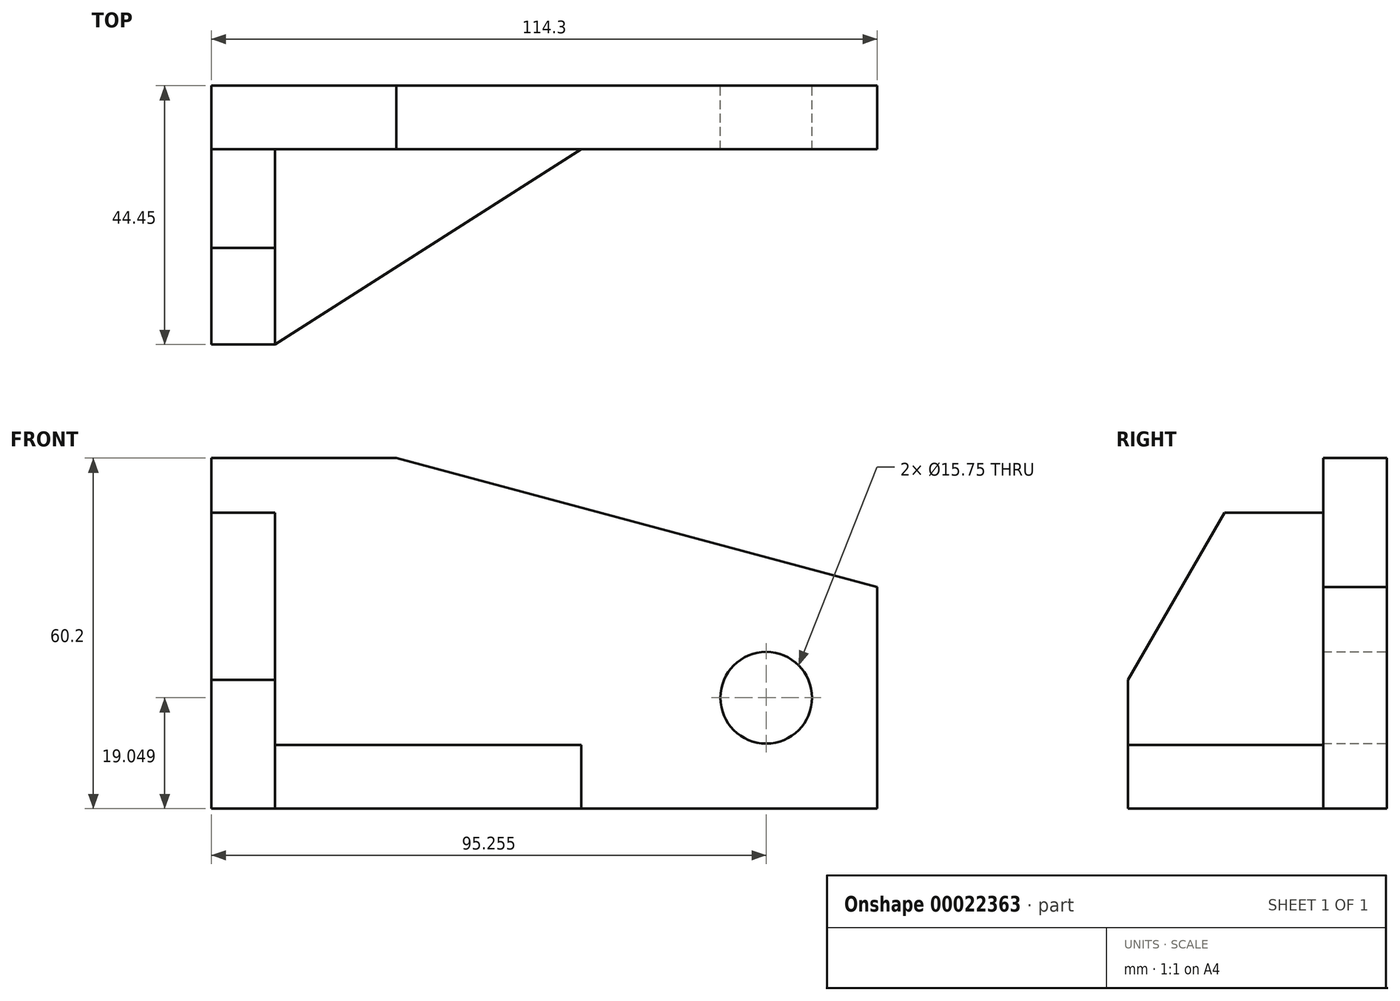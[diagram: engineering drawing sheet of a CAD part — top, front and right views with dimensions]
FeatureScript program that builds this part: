
annotation { "Feature Type Name" : "Feature", "Feature Type Description" : "" }
export const myFeature = defineFeature(function(context is Context, id is Id, definition is map)
    precondition{}
    {
        {
            var Q0;
            Q0=qCreatedBy(makeId("Front.planeOp"),FACE);
            var sketch = newSketch(context, id + "F0", { "sketchPlane" : qUnion([Q0])});
            skLineSegment(sketch, "E0.bottom", {"start": v(-54.92, 27.87) * mm, "end": v(-23.17, 27.87) * mm});
            skLineSegment(sketch, "E0.top", {"start": v(-54.92, -32.33) * mm, "end": v(59.38, -32.33) * mm});
            skLineSegment(sketch, "E0.left", {"start": v(-54.92, 27.87) * mm, "end": v(-54.92, -32.33) * mm});
            skLineSegment(sketch, "E0.right", {"start": v(59.38, 5.75) * mm, "end": v(59.38, -32.33) * mm});
            skLineSegment(sketch, "E1", {"start": v(-23.17, 27.87) * mm, "end": v(59.38, 5.75) * mm});
            skCircle(sketch, "E2", {"center": v(40.33, -13.28) * mm, "radius": 7.87 * mm});
            skSolve(sketch);
        }
        {
            var Q0;
            Q0=qSketchRegion(id+"F0",true);
            extrude(context, id + "F1", {"entities" : qUnion([Q0]), "depth" : 10.92 * mm});
        }
        {
            var Q0;
            Q0=makeQuery(id+"F1.opExtrude","SWEPT_FACE",FACE,{"disambiguationData":[OSD([sQuery(id+"F0.wireOp",EDGE,"E0.left")])]});
            var sketch = newSketch(context, id + "F2", { "sketchPlane" : qUnion([Q0])});
            skLineSegment(sketch, "E3.bottom", {"start": v(10.92, -32.33) * mm, "end": v(44.45, -32.33) * mm});
            skLineSegment(sketch, "E3.top", {"start": v(10.92, 18.47) * mm, "end": v(44.45, 18.47) * mm});
            skLineSegment(sketch, "E3.left", {"start": v(10.92, -32.33) * mm, "end": v(10.92, 18.47) * mm});
            skLineSegment(sketch, "E3.right", {"start": v(44.45, -32.33) * mm, "end": v(44.45, 18.47) * mm});
            skLineSegment(sketch, "E4", {"start": v(27.88, 18.47) * mm, "end": v(44.45, -10.23) * mm});
            skSolve(sketch);
        }
        {
            var Q0;
            {var subQ2=sQuery(id+"F2.wireOp",EDGE,"E3.bottom");Q0=makeQuery(id+"F2.imprint","IMPRINT",FACE,{"disambiguationData":[TD([[makeQuery(id+"F2.imprint","IMPRINT",EDGE,{"derivedFrom":subQ2}),1.0]])]});}
            extrude(context, id + "F3", {"entities" : qUnion([Q0]), "operationType" : NewBodyOperationType.ADD, "oppositeDirection" : true, "depth" : 10.92 * mm});
        }
        {
            var Q0;
            Q0=makeQuery(id+"F3.boolean.opBoolean","MERGE",FACE,{"derivedFrom":[makeQuery(id+"F1.opExtrude","SWEPT_FACE",FACE,{"disambiguationData":[OSD([sQuery(id+"F0.wireOp",EDGE,"E0.top")])]}),makeQuery(id+"F3.opExtrude","SWEPT_FACE",FACE,{"disambiguationData":[OSD([sQuery(id+"F2.wireOp",EDGE,"E3.bottom")])]})]});
            var sketch = newSketch(context, id + "F4", { "sketchPlane" : qUnion([Q0])});
            skLineSegment(sketch, "E5.bottom", {"start": v(-44, 44.45) * mm, "end": v(8.58, 44.45) * mm});
            skLineSegment(sketch, "E5.top", {"start": v(-44, 10.92) * mm, "end": v(8.58, 10.92) * mm});
            skLineSegment(sketch, "E5.left", {"start": v(-44, 44.45) * mm, "end": v(-44, 10.92) * mm});
            skLineSegment(sketch, "E5.right", {"start": v(8.58, 44.45) * mm, "end": v(8.58, 10.92) * mm});
            skLineSegment(sketch, "E6", {"start": v(-44, 44.45) * mm, "end": v(8.58, 10.92) * mm});
            skSolve(sketch);
        }
        {
            var Q0;
            Q0=makeQuery(id+"F4.imprint","IMPRINT",FACE,{"disambiguationData":[TD([[makeQuery(id+"F4.imprint","IMPRINT",EDGE,{"derivedFrom":sQuery(id+"F4.wireOp",EDGE,"E5.top")}),1.0]])]});
            extrude(context, id + "F5", {"entities" : qUnion([Q0]), "oppositeDirection" : true, "depth" : 10.92 * mm});
        }
        {
            var Q0;
            Q0=qSketchRegion(id+"F0",true);
            extrude(context, id + "F6", {"entities" : qUnion([Q0]), "depth" : 10.92 * mm});
        }
    });
